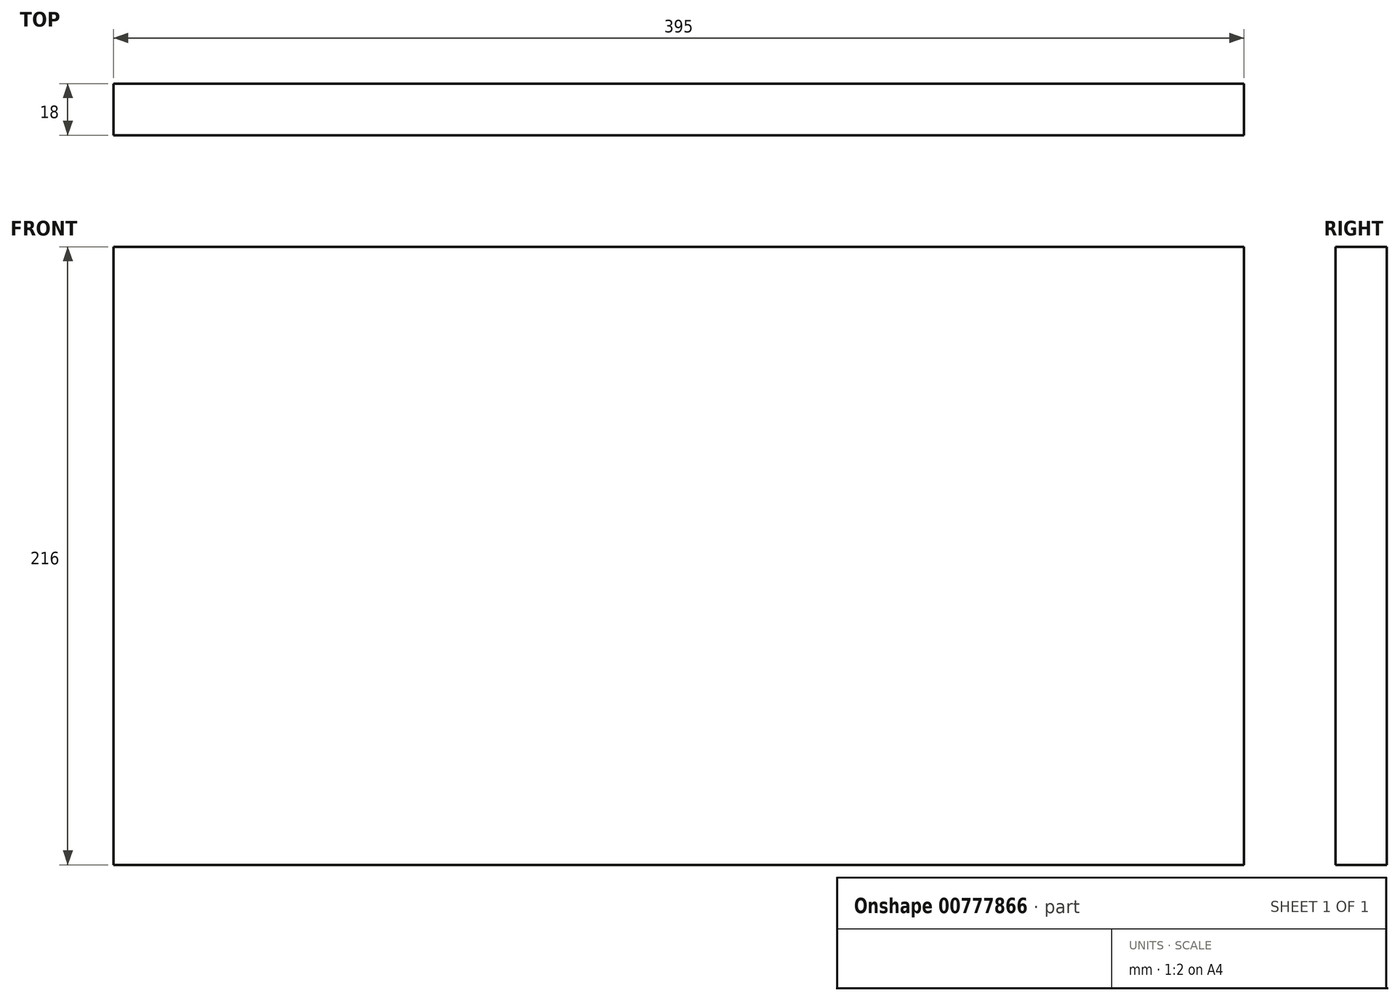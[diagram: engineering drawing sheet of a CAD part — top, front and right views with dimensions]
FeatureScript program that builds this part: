
annotation { "Feature Type Name" : "Feature", "Feature Type Description" : "" }
export const myFeature = defineFeature(function(context is Context, id is Id, definition is map)
    precondition{}
    {
        {
            var Q0;
            Q0=qCreatedBy(makeId("Front.planeOp"),FACE);
            var sketch = newSketch(context, id + "F0", { "sketchPlane" : qUnion([Q0])});
            skLineSegment(sketch, "E0.bottom", {"start": v(-197.5, 102.5) * mm, "end": v(197.5, 102.5) * mm});
            skLineSegment(sketch, "E0.top", {"start": v(-197.5, -113.5) * mm, "end": v(197.5, -113.5) * mm});
            skLineSegment(sketch, "E0.left", {"start": v(-197.5, 102.5) * mm, "end": v(-197.5, -113.5) * mm});
            skLineSegment(sketch, "E0.right", {"start": v(197.5, 102.5) * mm, "end": v(197.5, -113.5) * mm});
            skSolve(sketch);
        }
        {
            var Q0;
            Q0 = qSketchRegion(id + "F0", true);
            extrude(context, id + "F1", {"entities" : qUnion([Q0]), "depth" : 18 * mm, "offsetDistance" : 25 * mm});
        }
    });
